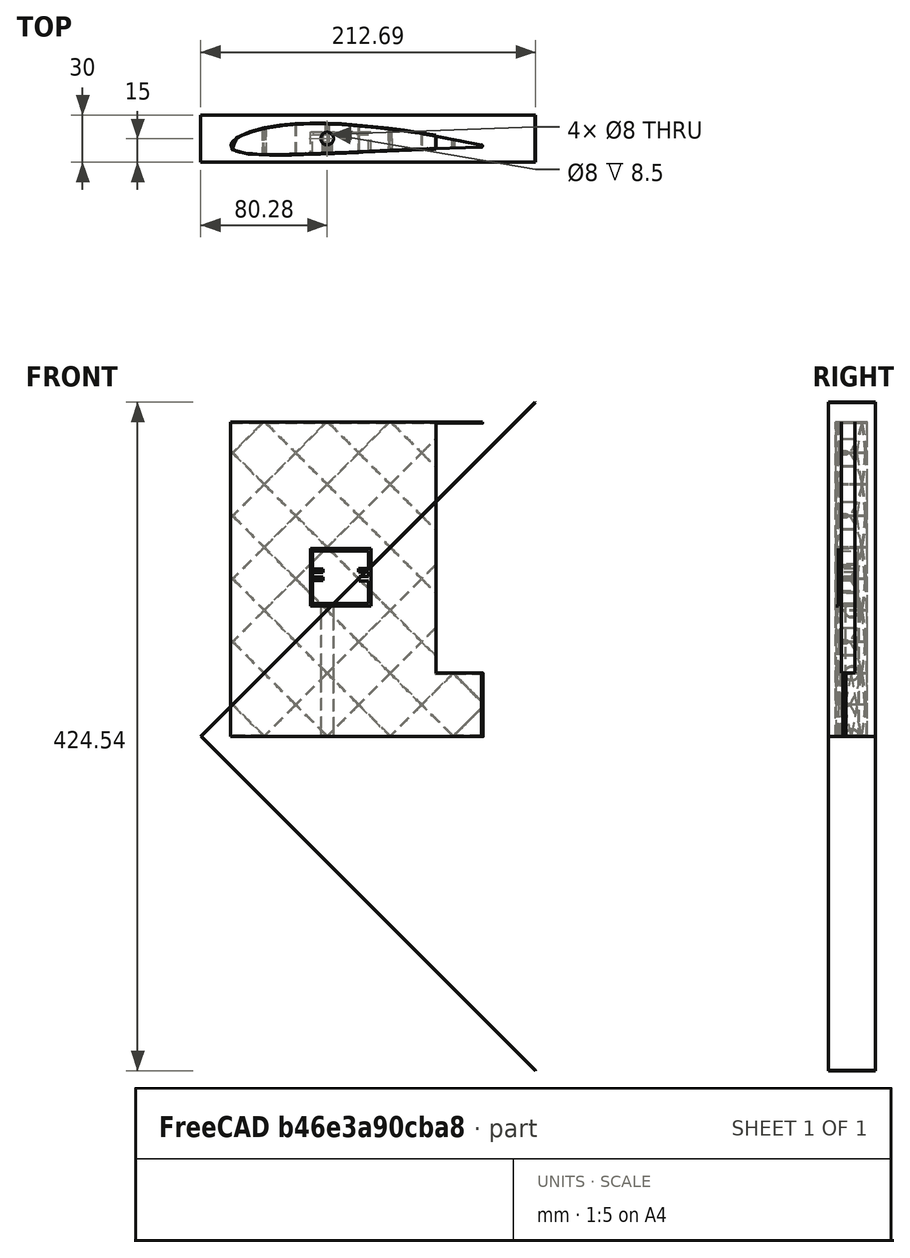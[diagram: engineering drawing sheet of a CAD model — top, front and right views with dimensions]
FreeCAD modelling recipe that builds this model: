
FCSTD DOCUMENT  (FreeCAD 0.21R33694 (Git))
Label: edge_wing
License: All rights reserved
LicenseURL: http://en.wikipedia.org/wiki/All_rights_reserved
objects: Sketcher::SketchObject×29, PartDesign::Pad×25, PartDesign::Body×19, Part::MultiFuse×13, Part::Cut×11, Part::MultiCommon×9, Part::Box×7, Part::Cylinder×7, PartDesign::Thickness×6, Part::FeaturePython×6, Part::Extrusion×2, PartDesign::FeatureBase×2
note: 161 computed .brp shape members not serialized (recipe doc carries the construction recipe); baked Part::Feature solids carry a one-line shape summary decoded from their .brp

FEATURE [Sketcher::SketchObject] Sketch006
  FullyConstrained = false
  MapMode = 5
  Support = -> [XY_Plane006]
  sketch-geometry (30):
    g0: ArcOfCircle CenterX=78.0455 CenterY=-4.69261 CenterZ=0 NormalX=0 NormalY=0 NormalZ=1 AngleXU=0 Radius=0.633228 StartAngle=4.68069 EndAngle=7.80443
    g1-g15: Circle x15 (B-spline internal-alignment scaffolding for g16; pole/knot coordinates omitted)
    g16: BSplineCurve PolesCount=15 KnotsCount=13 Degree=3 IsPeriodic=0
    g17-g29: GeomPoint x13 (B-spline internal-alignment scaffolding for g16; pole/knot coordinates omitted)
  constraints (6):
    c: Weight(g1) = 1
    c: Coincident(g16,g0)
    c: Equal(g1, g2-g15) x14
    c: Coincident(g16,g0)
    c: InternalAlignment(g1-g15 -> g16) x15
    c: InternalAlignment(g17-g29 -> g16) x13
FEATURE [PartDesign::Pad] Pad006
  Direction = (0,0,1)
  Length = 200
  Length2 = 10
  Profile = -> Sketch006
  ReferenceAxis = -> Sketch006 [N_Axis]
  Type = 0
FEATURE [PartDesign::Thickness] Thickness002
  Base = -> Pad006 [Face4,Face3]
  BaseFeature = -> Pad006
  Intersection = false
  Join = 0
  Mode = 1
  SupportTransform = false
  Value = 0.4
FEATURE [PartDesign::Body] Body006
  Group = -> [Sketch006,Pad006,Thickness002]
  Origin = -> Origin006
  Tip = -> Thickness002
FEATURE [Sketcher::SketchObject] Sketch007
  FullyConstrained = false
  MapMode = 5
  Support = -> [XY_Plane007]
  sketch-geometry (30):
    g0: ArcOfCircle CenterX=78.0455 CenterY=-4.69261 CenterZ=0 NormalX=0 NormalY=0 NormalZ=1 AngleXU=0 Radius=0.633228 StartAngle=4.68069 EndAngle=7.80443
    g1-g15: Circle x15 (B-spline internal-alignment scaffolding for g16; pole/knot coordinates omitted)
    g16: BSplineCurve PolesCount=15 KnotsCount=13 Degree=3 IsPeriodic=0
    g17-g29: GeomPoint x13 (B-spline internal-alignment scaffolding for g16; pole/knot coordinates omitted)
  constraints (6):
    c: Weight(g1) = 1
    c: Coincident(g16,g0)
    c: Equal(g1, g2-g15) x14
    c: Coincident(g16,g0)
    c: InternalAlignment(g1-g15 -> g16) x15
    c: InternalAlignment(g17-g29 -> g16) x13
FEATURE [PartDesign::Pad] Pad007
  Direction = (0,0,1)
  Length = 200
  Length2 = 10
  Profile = -> Sketch007
  ReferenceAxis = -> Sketch007 [N_Axis]
  Type = 0
FEATURE [PartDesign::Body] Body007
  Group = -> [Sketch007,Pad007]
  Origin = -> Origin007
  Tip = -> Pad007
FEATURE [Part::Box] Box004  label="Cube004"
  AttacherType = Attacher::AttachEngine3D
  Height = 0.4
  Length = 300
  Placement = pos=(-100,-15,0) rot=(0,1,0;0.785398rad)
  Width = 30
FEATURE [Part::FeaturePython] Array006  # Draft array (typed FeaturePython)
  AlwaysSyncPlacement = false
  Angle = 360
  ArrayType = 0
  Axis = (0,0,1)
  Base = -> Box004
  Center = (0,0,0)
  Count = 10
  ExpandArray = false
  Fuse = false
  IntervalAxis = (0,0,0)
  IntervalX = (100,0,0)
  IntervalY = (0,100,0)
  IntervalZ = (0,0,40)
  NumberCircles = 3
  NumberPolar = 5
  NumberX = 1
  NumberY = 1
  NumberZ = 10
  PlacementList = 10 placements: arithmetic series from (-100,-15,0) step (0,0,40) to (-100,-15,360)
  RadialDistance = 50
  ScaleList = (10) [(1,1,1),(1,1,1),(1,1,1),(1,1,1),(1,1,1),(1,1,1),(1,1,1),(1,1,1),(1,1,1),(1,1,1)]
  Symmetry = 1
  TangentialDistance = 25
FEATURE [Part::FeaturePython] Array007  # Draft array (typed FeaturePython)
  AlwaysSyncPlacement = false
  Angle = 360
  ArrayType = 0
  Axis = (0,0,1)
  Base = -> Array006
  Center = (0,0,0)
  Count = 9
  ExpandArray = false
  Fuse = false
  IntervalAxis = (0,0,0)
  IntervalX = (100,0,0)
  IntervalY = (0,100,0)
  IntervalZ = (0,0,40)
  NumberCircles = 3
  NumberPolar = 5
  NumberX = 1
  NumberY = 1
  NumberZ = 9
  PlacementList = 9 placements: arithmetic series from (0,0,0) step (0,0,40) to (0,0,320)
  RadialDistance = 50
  ScaleList = (9) [(1,1,1),(1,1,1),(1,1,1),(1,1,1),(1,1,1),(1,1,1),(1,1,1),(1,1,1),(1,1,1)]
  Symmetry = 1
  TangentialDistance = 25
FEATURE [Part::MultiCommon] Common005
  Shapes = -> [Body007,Array007]
FEATURE [Sketcher::SketchObject] Sketch008
  FullyConstrained = false
  MapMode = 5
  Support = -> [XY_Plane008]
  sketch-geometry (30):
    g0: ArcOfCircle CenterX=78.0455 CenterY=-4.69261 CenterZ=0 NormalX=0 NormalY=0 NormalZ=1 AngleXU=0 Radius=0.633228 StartAngle=4.68069 EndAngle=7.80443
    g1-g15: Circle x15 (B-spline internal-alignment scaffolding for g16; pole/knot coordinates omitted)
    g16: BSplineCurve PolesCount=15 KnotsCount=13 Degree=3 IsPeriodic=0
    g17-g29: GeomPoint x13 (B-spline internal-alignment scaffolding for g16; pole/knot coordinates omitted)
  constraints (6):
    c: Weight(g1) = 1
    c: Coincident(g16,g0)
    c: Equal(g1, g2-g15) x14
    c: Coincident(g16,g0)
    c: InternalAlignment(g1-g15 -> g16) x15
    c: InternalAlignment(g17-g29 -> g16) x13
FEATURE [PartDesign::Pad] Pad008
  Direction = (0,0,1)
  Length = 200
  Length2 = 10
  Profile = -> Sketch008
  ReferenceAxis = -> Sketch008 [N_Axis]
  Type = 0
FEATURE [PartDesign::Body] Body008
  Group = -> [Sketch008,Pad008]
  Origin = -> Origin008
  Tip = -> Pad008
FEATURE [Part::Box] Box005  label="Cube005"
  AttacherType = Attacher::AttachEngine3D
  Height = 0.4
  Length = 300
  Placement = pos=(-100,-15,0) rot=(0,-1,0;0.785398rad)
  Width = 30
FEATURE [Part::FeaturePython] Array008  # Draft array (typed FeaturePython)
  AlwaysSyncPlacement = false
  Angle = 360
  ArrayType = 0
  Axis = (0,0,1)
  Base = -> Box005
  Center = (0,0,0)
  Count = 20
  ExpandArray = false
  Fuse = false
  IntervalAxis = (0,0,0)
  IntervalX = (100,0,0)
  IntervalY = (0,100,0)
  IntervalZ = (0,0,40)
  NumberCircles = 3
  NumberPolar = 5
  NumberX = 1
  NumberY = 1
  NumberZ = 20
  Placement = pos=(0,1.90735e-05,-160) rot=(0,0,1;0rad)
  PlacementList = 20 placements: arithmetic series from (-100,-15,0) step (0,0,40) to (-100,-15,760)
  RadialDistance = 50
  ScaleList = (20) [(1,1,1),(1,1,1),(1,1,1),(1,1,1),(1,1,1),(1,1,1),(1,1,1),(1,1,1),(1,1,1),(1,1,1),(1,1,1),(1,1,1),(1,1,1),(1,1,1),(1,1,1),(1,1,1),(1,1,1),(1,1,1),(1,1,1),(1,1,1)]
  Symmetry = 1
  TangentialDistance = 25
FEATURE [Part::MultiCommon] Common004
  Shapes = -> [Body008,Array008]
FEATURE [Part::MultiFuse] Fusion004
  Shapes = -> [Common005,Common004]
FEATURE [Part::MultiFuse] Fusion005
  Shapes = -> [Body006,Fusion004]
FEATURE [Sketcher::SketchObject] Sketch015
  FullyConstrained = false
  MapMode = 5
  Placement = pos=(0,0,0) rot=(1,0,0;1.5708rad)
  sketch-geometry (4):
    g0: LineSegment StartX=0.4 StartY=0 StartZ=0 EndX=187.784 EndY=0 EndZ=0
    g1: LineSegment StartX=187.784 StartY=0 StartZ=0 EndX=187.784 EndY=-55.3386 EndZ=0
    g2: LineSegment StartX=187.784 StartY=-55.3386 StartZ=0 EndX=0.4 EndY=-55.3386 EndZ=0
    g3: LineSegment StartX=0.4 StartY=-55.3386 StartZ=0 EndX=0.4 EndY=0 EndZ=0
  constraints (8):
    c: Coincident(g0,g1)
    c: Coincident(g1,g2)
    c: Coincident(g2,g3)
    c: Coincident(g3,g0)
    c: Horizontal(g0)
    c: Horizontal(g2)
    c: Vertical(g1)
    c: Vertical(g3)
FEATURE [Part::Extrusion] Extrude
  Base = -> Sketch015
  Dir = (0,-1,-2e-16)
  DirMode = 2
  FaceMakerClass = Part::FaceMakerBullseye
  LengthFwd = 43
  LengthRev = 0
  Placement = pos=(49,20,40) rot=(0,-1,0;1.5708rad)
  Solid = true
  Symmetric = false
FEATURE [Part::Cut] Cut
  Base = -> Fusion005
  Tool = -> Extrude
FEATURE [Sketcher::SketchObject] Sketch010
  FullyConstrained = true
  MapMode = 5
  Support = -> [XY_Plane010]
  sketch-geometry (4):
    g0: LineSegment StartX=0 StartY=0 StartZ=0 EndX=160 EndY=0 EndZ=0
    g1: LineSegment StartX=160 StartY=0 StartZ=0 EndX=160 EndY=30 EndZ=0
    g2: LineSegment StartX=160 StartY=30 StartZ=0 EndX=0 EndY=30 EndZ=0
    g3: LineSegment StartX=0 StartY=30 StartZ=0 EndX=0 EndY=0 EndZ=0
  constraints (11):
    c: Coincident(g0,g1)
    c: Coincident(g1,g2)
    c: Coincident(g2,g3)
    c: Coincident(g3,g0)
    c: Horizontal(g0)
    c: Horizontal(g2)
    c: Vertical(g1)
    c: Vertical(g3)
    c: Coincident(g0,g-1)
    c: DistanceX(g2,g2) = 160
    c: DistanceY(g1,g1) = 30
FEATURE [PartDesign::Pad] Pad010
  Direction = (0,0,1)
  Length = 0.4
  Length2 = 10
  Profile = -> Sketch010
  ReferenceAxis = -> Sketch010 [N_Axis]
  Type = 0
FEATURE [Sketcher::SketchObject] Sketch011
  ExternalGeometry = -> [Pad010]
  FullyConstrained = true
  MapMode = 5
  Placement = pos=(0,0,0) rot=(1,0,0;3.14159rad)
  Support = -> [Pad010]
  sketch-geometry (4):
    g0: LineSegment StartX=0 StartY=0 StartZ=0 EndX=0.4 EndY=0 EndZ=0
    g1: LineSegment StartX=0.4 StartY=0 StartZ=0 EndX=0.4 EndY=-30 EndZ=0
    g2: LineSegment StartX=0.4 StartY=-30 StartZ=0 EndX=0 EndY=-30 EndZ=0
    g3: LineSegment StartX=0 StartY=-30 StartZ=0 EndX=0 EndY=0 EndZ=0
  constraints (11):
    c: Coincident(g0,g1)
    c: Coincident(g1,g2)
    c: Coincident(g2,g3)
    c: Coincident(g3,g0)
    c: Horizontal(g0)
    c: Horizontal(g2)
    c: Vertical(g1)
    c: Vertical(g3)
    c: Coincident(g0,g-1)
    c: DistanceY(g-3,g2) = 0
    c: DistanceX(g0,g0) = 0.4
FEATURE [PartDesign::Pad] Pad011
  BaseFeature = -> Pad010
  Direction = (0,0,-1)
  Length = 30
  Length2 = 10
  Profile = -> Sketch011
  ReferenceAxis = -> Sketch011 [N_Axis]
  Type = 0
FEATURE [Sketcher::SketchObject] Sketch014
  FullyConstrained = true
  MapMode = 5
  Placement = pos=(0,0,0) rot=(1,0,0;1.5708rad)
  Support = -> [XZ_Plane009]
FEATURE [PartDesign::Body] Body009
  Group = -> [Sketch010,Pad010,Sketch011,Pad011,Sketch014]
  Origin = -> Origin009
  Placement = pos=(49,-16,40) rot=(0,-1,0;1.5708rad)
  Tip = -> Pad011
FEATURE [Sketcher::SketchObject] Sketch009
  FullyConstrained = false
  MapMode = 5
  sketch-geometry (30):
    g0: ArcOfCircle CenterX=78.0455 CenterY=-4.69261 CenterZ=0 NormalX=0 NormalY=0 NormalZ=1 AngleXU=0 Radius=0.633228 StartAngle=4.68069 EndAngle=7.80443
    g1-g15: Circle x15 (B-spline internal-alignment scaffolding for g16; pole/knot coordinates omitted)
    g16: BSplineCurve PolesCount=15 KnotsCount=13 Degree=3 IsPeriodic=0
    g17-g29: GeomPoint x13 (B-spline internal-alignment scaffolding for g16; pole/knot coordinates omitted)
  constraints (6):
    c: Weight(g1) = 1
    c: Coincident(g16,g0)
    c: Equal(g1, g2-g15) x14
    c: Coincident(g16,g0)
    c: InternalAlignment(g1-g15 -> g16) x15
    c: InternalAlignment(g17-g29 -> g16) x13
FEATURE [PartDesign::Pad] Pad009
  Direction = (0,0,1)
  Length = 200
  Length2 = 10
  Profile = -> Sketch009
  ReferenceAxis = -> Sketch009 [N_Axis]
  Type = 0
FEATURE [Part::MultiCommon] Common006
  Shapes = -> [Body009,Pad009]
FEATURE [Part::MultiFuse] Fusion006
  Shapes = -> [Cut,Common006]
FEATURE [Sketcher::SketchObject] Sketch018
  FullyConstrained = false
  MapMode = 5
  Support = -> [XY_Plane002]
  sketch-geometry (4):
    g0: LineSegment StartX=-7.74956 StartY=27.0881 StartZ=0 EndX=30.8607 EndY=27.0881 EndZ=0
    g1: LineSegment StartX=30.8607 StartY=27.0881 StartZ=0 EndX=30.8607 EndY=-9.4314 EndZ=0
    g2: LineSegment StartX=30.8607 StartY=-9.4314 StartZ=0 EndX=-7.74956 EndY=-9.4314 EndZ=0
    g3: LineSegment StartX=-7.74956 StartY=-9.4314 StartZ=0 EndX=-7.74956 EndY=27.0881 EndZ=0
  constraints (8):
    c: Coincident(g0,g1)
    c: Coincident(g1,g2)
    c: Coincident(g2,g3)
    c: Coincident(g3,g0)
    c: Horizontal(g0)
    c: Horizontal(g2)
    c: Vertical(g1)
    c: Vertical(g3)
FEATURE [PartDesign::Pad] Pad012
  Direction = (0,0,1)
  Length = 14
  Length2 = 10
  Profile = -> Sketch018
  ReferenceAxis = -> Sketch018 [N_Axis]
  Type = 0
FEATURE [PartDesign::Body] Body002
  Group = -> [Sketch018,Pad012]
  Origin = -> Origin002
  Placement = pos=(0,4,110) rot=(0,0.707107,-0.707107;3.14159rad)
  Tip = -> Pad012
FEATURE [Sketcher::SketchObject] Sketch017
  FullyConstrained = false
  MapMode = 5
  Support = -> [XY_Plane001]
  sketch-geometry (4):
    g0: LineSegment StartX=-7.74956 StartY=27.0881 StartZ=0 EndX=30.8607 EndY=27.0881 EndZ=0
    g1: LineSegment StartX=30.8607 StartY=27.0881 StartZ=0 EndX=30.8607 EndY=-9.4314 EndZ=0
    g2: LineSegment StartX=30.8607 StartY=-9.4314 StartZ=0 EndX=-7.74956 EndY=-9.4314 EndZ=0
    g3: LineSegment StartX=-7.74956 StartY=-9.4314 StartZ=0 EndX=-7.74956 EndY=27.0881 EndZ=0
  constraints (8):
    c: Coincident(g0,g1)
    c: Coincident(g1,g2)
    c: Coincident(g2,g3)
    c: Coincident(g3,g0)
    c: Horizontal(g0)
    c: Horizontal(g2)
    c: Vertical(g1)
    c: Vertical(g3)
FEATURE [PartDesign::Pad] Pad013
  Direction = (0,0,1)
  Length = 14
  Length2 = 10
  Profile = -> Sketch017
  ReferenceAxis = -> Sketch017 [N_Axis]
  Type = 0
FEATURE [PartDesign::Thickness] Thickness
  Base = -> Pad013 [Face6]
  BaseFeature = -> Pad013
  Intersection = false
  Join = 1
  Mode = 0
  Reversed = true
  SupportTransform = false
  Value = 1.6
FEATURE [Sketcher::SketchObject] Sketch021
  ExternalGeometry = -> [Thickness]
  FullyConstrained = false
  MapMode = 5
  Placement = pos=(0,0,1.6) rot=(0,0,1;0rad)
  Support = -> [Thickness]
  sketch-geometry (16):
    g0: LineSegment StartX=-6.14956 StartY=10.9638 StartZ=0 EndX=-0.106128 EndY=10.9638 EndZ=0
    g1: LineSegment StartX=-0.106128 StartY=10.9638 StartZ=0 EndX=-0.106128 EndY=8.15304 EndZ=0
    g2: LineSegment StartX=-0.106128 StartY=8.15304 StartZ=0 EndX=-6.14956 EndY=8.15304 EndZ=0
    g3: LineSegment StartX=-6.14956 StartY=8.15304 StartZ=0 EndX=-6.14956 EndY=10.9638 EndZ=0
    g4: LineSegment StartX=-6.14956 StartY=3.3087 StartZ=0 EndX=0 EndY=3.3087 EndZ=0
    g5: LineSegment StartX=0 StartY=3.3087 StartZ=0 EndX=0 EndY=5.33627 EndZ=0
    g6: LineSegment StartX=0 StartY=5.33627 StartZ=0 EndX=-6.14956 EndY=5.33627 EndZ=0
    g7: LineSegment StartX=-6.14956 StartY=5.33627 StartZ=0 EndX=-6.14956 EndY=3.3087 EndZ=0
    g8: LineSegment StartX=29.2607 StartY=10.6733 StartZ=0 EndX=22.6404 EndY=10.6733 EndZ=0
    g9: LineSegment StartX=22.6404 StartY=10.6733 StartZ=0 EndX=22.6404 EndY=8.47828 EndZ=0
    g10: LineSegment StartX=22.6404 StartY=8.47828 StartZ=0 EndX=29.2607 EndY=8.47828 EndZ=0
    g11: LineSegment StartX=29.2607 StartY=8.47828 StartZ=0 EndX=29.2607 EndY=10.6733 EndZ=0
    g12: LineSegment StartX=29.2607 StartY=5.57967 StartZ=0 EndX=22.6404 EndY=5.57967 EndZ=0
    g13: LineSegment StartX=22.6404 StartY=5.57967 StartZ=0 EndX=22.6404 EndY=3.49718 EndZ=0
    g14: LineSegment StartX=22.6404 StartY=3.49718 StartZ=0 EndX=29.2607 EndY=3.49718 EndZ=0
    g15: LineSegment StartX=29.2607 StartY=3.49718 StartZ=0 EndX=29.2607 EndY=5.57967 EndZ=0
  constraints (37):
    c: Coincident(g0,g1)
    c: Coincident(g1,g2)
    c: Coincident(g2,g3)
    c: Coincident(g3,g0)
    c: Horizontal(g0)
    c: Horizontal(g2)
    c: Vertical(g1)
    c: Vertical(g3)
    c: PointOnObject(g0,g-3)
    c: Coincident(g4,g5)
    c: Coincident(g5,g6)
    c: Coincident(g6,g7)
    c: Coincident(g7,g4)
    c: Horizontal(g4)
    c: Horizontal(g6)
    c: Vertical(g5)
    c: Vertical(g7)
    c: PointOnObject(g4,g-3)
    c: PointOnObject(g5,g-2)
    c: Coincident(g8,g9)
    c: Coincident(g9,g10)
    c: Coincident(g10,g11)
    c: Coincident(g11,g8)
    c: Horizontal(g8)
    c: Horizontal(g10)
    c: Vertical(g9)
    c: Vertical(g11)
    c: PointOnObject(g8,g-4)
    c: Coincident(g12,g13)
    c: Coincident(g13,g14)
    c: Coincident(g14,g15)
    c: Coincident(g15,g12)
    c: Horizontal(g12)
    c: Horizontal(g14)
    c: Vertical(g13)
    c: Vertical(g15)
    c: PointOnObject(g12,g-4)
FEATURE [PartDesign::Pad] Pad014
  BaseFeature = -> Thickness
  Direction = (0,0,1)
  Length = 12.4
  Length2 = 10
  Profile = -> Sketch021
  ReferenceAxis = -> Sketch021 [N_Axis]
  Type = 0
FEATURE [PartDesign::Body] Body001
  Group = -> [Sketch017,Pad013,Thickness,Sketch021,Pad014]
  Origin = -> Origin001
  Placement = pos=(0,4,110) rot=(0,-0.707107,0.707107;3.14159rad)
  Tip = -> Pad014
FEATURE [Part::Cut] Cut001
  Base = -> Fusion006
  Tool = -> Body002
FEATURE [Sketcher::SketchObject] Sketch022
  FullyConstrained = false
  MapMode = 5
  Support = -> [XY_Plane011]
  sketch-geometry (30):
    g0: ArcOfCircle CenterX=78.0455 CenterY=-4.69261 CenterZ=0 NormalX=0 NormalY=0 NormalZ=1 AngleXU=0 Radius=0.633228 StartAngle=4.68069 EndAngle=7.80443
    g1-g15: Circle x15 (B-spline internal-alignment scaffolding for g16; pole/knot coordinates omitted)
    g16: BSplineCurve PolesCount=15 KnotsCount=13 Degree=3 IsPeriodic=0
    g17-g29: GeomPoint x13 (B-spline internal-alignment scaffolding for g16; pole/knot coordinates omitted)
  constraints (6):
    c: Weight(g1) = 1
    c: Coincident(g16,g0)
    c: Equal(g1, g2-g15) x14
    c: Coincident(g16,g0)
    c: InternalAlignment(g1-g15 -> g16) x15
    c: InternalAlignment(g17-g29 -> g16) x13
FEATURE [PartDesign::Pad] Pad015
  Direction = (0,0,1)
  Length = 200
  Length2 = 10
  Profile = -> Sketch022
  ReferenceAxis = -> Sketch022 [N_Axis]
  Type = 0
FEATURE [Part::MultiCommon] Common
  Shapes = -> [Body001,Pad015]
FEATURE [Part::Cylinder] Cylinder003
  Angle = 360
  AttacherType = Attacher::AttachEngine3D
  FirstAngle = 0
  Height = 84.5
  Placement = pos=(-20,0,0) rot=(0,0,1;0rad)
  Radius = 4
  SecondAngle = 0
FEATURE [PartDesign::FeatureBase] BaseFeature
  BaseFeature = -> Cylinder003
FEATURE [PartDesign::Thickness] Thickness001
  Base = -> BaseFeature [Face3,Face2]
  BaseFeature = -> BaseFeature
  Intersection = false
  Join = 0
  Mode = 1
  SupportTransform = false
  Value = 0.4
FEATURE [PartDesign::Body] Body003
  BaseFeature = -> Cylinder003
  Group = -> [BaseFeature,Thickness001]
  Origin = -> Origin003
  Placement = pos=(-20,0,0) rot=(0,0,1;0rad)
  Tip = -> Thickness001
FEATURE [Part::Cylinder] Cylinder002
  Angle = 360
  AttacherType = Attacher::AttachEngine3D
  FirstAngle = 0
  Height = 200
  Placement = pos=(-20,0,0) rot=(0,0,1;0rad)
  Radius = 4
  SecondAngle = 0
FEATURE [Sketcher::SketchObject] Sketch004
  FullyConstrained = false
  MapMode = 5
  Support = -> [XY_Plane005]
  sketch-geometry (30):
    g0: ArcOfCircle CenterX=78.0455 CenterY=-4.69261 CenterZ=0 NormalX=0 NormalY=0 NormalZ=1 AngleXU=0 Radius=0.633228 StartAngle=4.68069 EndAngle=7.80443
    g1-g15: Circle x15 (B-spline internal-alignment scaffolding for g16; pole/knot coordinates omitted)
    g16: BSplineCurve PolesCount=15 KnotsCount=13 Degree=3 IsPeriodic=0
    g17-g29: GeomPoint x13 (B-spline internal-alignment scaffolding for g16; pole/knot coordinates omitted)
  constraints (6):
    c: Weight(g1) = 1
    c: Coincident(g16,g0)
    c: Equal(g1, g2-g15) x14
    c: Coincident(g16,g0)
    c: InternalAlignment(g1-g15 -> g16) x15
    c: InternalAlignment(g17-g29 -> g16) x13
FEATURE [PartDesign::Pad] Pad004
  Direction = (1,1,1)
  Length = 0.8
  Length2 = 100
  Profile = -> Sketch004
  Type = 0
FEATURE [PartDesign::Body] Body005
  Group = -> [Sketch004,Pad004]
  Origin = -> Origin005
  Tip = -> Pad004
FEATURE [Part::Cut] Cut002
  Base = -> Body005
  Placement = pos=(0,0,199.2) rot=(0,0,1;0rad)
  Tool = -> Cylinder002
FEATURE [Part::Cylinder] Cylinder001
  Angle = 360
  AttacherType = Attacher::AttachEngine3D
  FirstAngle = 0
  Height = 200
  Placement = pos=(-20,0,0) rot=(0,0,1;0rad)
  Radius = 4
  SecondAngle = 0
FEATURE [Sketcher::SketchObject] Sketch003
  FullyConstrained = false
  MapMode = 5
  Support = -> [XY_Plane004]
  sketch-geometry (30):
    g0: ArcOfCircle CenterX=78.0455 CenterY=-4.69261 CenterZ=0 NormalX=0 NormalY=0 NormalZ=1 AngleXU=0 Radius=0.633228 StartAngle=4.68069 EndAngle=7.80443
    g1-g15: Circle x15 (B-spline internal-alignment scaffolding for g16; pole/knot coordinates omitted)
    g16: BSplineCurve PolesCount=15 KnotsCount=13 Degree=3 IsPeriodic=0
    g17-g29: GeomPoint x13 (B-spline internal-alignment scaffolding for g16; pole/knot coordinates omitted)
  constraints (6):
    c: Weight(g1) = 1
    c: Coincident(g16,g0)
    c: Equal(g1, g2-g15) x14
    c: Coincident(g16,g0)
    c: InternalAlignment(g1-g15 -> g16) x15
    c: InternalAlignment(g17-g29 -> g16) x13
FEATURE [PartDesign::Pad] Pad003
  Direction = (1,1,1)
  Length = 0.8
  Length2 = 100
  Profile = -> Sketch003
  Type = 0
FEATURE [PartDesign::Body] Body004
  Group = -> [Sketch003,Pad003]
  Origin = -> Origin004
  Tip = -> Pad003
FEATURE [Part::Cut] Cut003
  Base = -> Body004
  Tool = -> Cylinder001
FEATURE [Part::MultiFuse] Fusion
  Shapes = -> [Common,Cut001]
FEATURE [Part::Cylinder] Cylinder004
  Angle = 360
  AttacherType = Attacher::AttachEngine3D
  FirstAngle = 0
  Height = 84.5
  Placement = pos=(-20,0,0) rot=(0,0,1;0rad)
  Radius = 4
  SecondAngle = 0
FEATURE [Part::Cut] Cut004
  Base = -> Fusion
  Tool = -> Cylinder004
FEATURE [Part::Box] Box  label="Cube"
  AttacherType = Attacher::AttachEngine3D
  Height = 20
  Length = 40
  Placement = pos=(49,-7,196) rot=(0,0,1;0rad)
  Width = 10
FEATURE [Sketcher::SketchObject] Sketch023
  FullyConstrained = false
  MapMode = 5
  Support = -> [XY_Plane012]
  sketch-geometry (30):
    g0: ArcOfCircle CenterX=78.0455 CenterY=-4.69261 CenterZ=0 NormalX=0 NormalY=0 NormalZ=1 AngleXU=0 Radius=0.633228 StartAngle=4.68069 EndAngle=7.80443
    g1-g15: Circle x15 (B-spline internal-alignment scaffolding for g16; pole/knot coordinates omitted)
    g16: BSplineCurve PolesCount=15 KnotsCount=13 Degree=3 IsPeriodic=0
    g17-g29: GeomPoint x13 (B-spline internal-alignment scaffolding for g16; pole/knot coordinates omitted)
  constraints (6):
    c: Weight(g1) = 1
    c: Coincident(g16,g0)
    c: Equal(g1, g2-g15) x14
    c: Coincident(g16,g0)
    c: InternalAlignment(g1-g15 -> g16) x15
    c: InternalAlignment(g17-g29 -> g16) x13
FEATURE [PartDesign::Pad] Pad016
  Direction = (1,1,1)
  Length = 0.8
  Length2 = 100
  Profile = -> Sketch023
  Type = 0
FEATURE [PartDesign::Body] Body010
  Group = -> [Sketch023,Pad016]
  Origin = -> Origin010
  Placement = pos=(0,0,199.2) rot=(0,0,1;0rad)
  Tip = -> Pad016
FEATURE [Part::Cut] Cut005
  Base = -> Body010
  Tool = -> Box
FEATURE [Part::MultiFuse] Fusion007
  Shapes = -> [Cut005,Cut003,Cut004]
FEATURE [Part::MultiFuse] Fusion008
  Shapes = -> [Body003,Fusion007]
FEATURE [Part::Box] Box006  label="Cube006"
  AttacherType = Attacher::AttachEngine3D
  Height = 0.8
  Length = 50
  Placement = pos=(48.6,-10.8,39.6) rot=(0,0,1;0rad)
  Width = 30
FEATURE [Part::Box] Box007  label="Cube007"
  AttacherType = Attacher::AttachEngine3D
  Height = 20
  Length = 40
  Placement = pos=(49,-7,196) rot=(0,0,1;0rad)
  Width = 10
FEATURE [Part::Box] Box008  label="Cube008"
  AttacherType = Attacher::AttachEngine3D
  Height = 0.4
  Length = 300
  Placement = pos=(-100,-15,0) rot=(0,1,0;0.785398rad)
  Width = 30
FEATURE [Part::FeaturePython] Array009  # Draft array (typed FeaturePython)
  AlwaysSyncPlacement = false
  Angle = 360
  ArrayType = 0
  Axis = (0,0,1)
  Base = -> Box008
  Center = (0,0,0)
  Count = 10
  ExpandArray = false
  Fuse = false
  IntervalAxis = (0,0,0)
  IntervalX = (100,0,0)
  IntervalY = (0,100,0)
  IntervalZ = (0,0,40)
  NumberCircles = 3
  NumberPolar = 5
  NumberX = 1
  NumberY = 1
  NumberZ = 10
  PlacementList = 10 placements: arithmetic series from (-100,-15,0) step (0,0,40) to (-100,-15,360)
  RadialDistance = 50
  ScaleList = (10) [(1,1,1),(1,1,1),(1,1,1),(1,1,1),(1,1,1),(1,1,1),(1,1,1),(1,1,1),(1,1,1),(1,1,1)]
  Symmetry = 1
  TangentialDistance = 25
FEATURE [Part::FeaturePython] Array010  # Draft array (typed FeaturePython)
  AlwaysSyncPlacement = false
  Angle = 360
  ArrayType = 0
  Axis = (0,0,1)
  Base = -> Array009
  Center = (0,0,0)
  Count = 9
  ExpandArray = false
  Fuse = false
  IntervalAxis = (0,0,0)
  IntervalX = (100,0,0)
  IntervalY = (0,100,0)
  IntervalZ = (0,0,40)
  NumberCircles = 3
  NumberPolar = 5
  NumberX = 1
  NumberY = 1
  NumberZ = 9
  PlacementList = 9 placements: arithmetic series from (0,0,0) step (0,0,40) to (0,0,320)
  RadialDistance = 50
  ScaleList = (9) [(1,1,1),(1,1,1),(1,1,1),(1,1,1),(1,1,1),(1,1,1),(1,1,1),(1,1,1),(1,1,1)]
  Symmetry = 1
  TangentialDistance = 25
FEATURE [Part::Box] Box009  label="Cube009"
  AttacherType = Attacher::AttachEngine3D
  Height = 0.4
  Length = 300
  Placement = pos=(-100,-15,0) rot=(0,-1,0;0.785398rad)
  Width = 30
FEATURE [Part::FeaturePython] Array011  # Draft array (typed FeaturePython)
  AlwaysSyncPlacement = false
  Angle = 360
  ArrayType = 0
  Axis = (0,0,1)
  Base = -> Box009
  Center = (0,0,0)
  Count = 20
  ExpandArray = false
  Fuse = false
  IntervalAxis = (0,0,0)
  IntervalX = (100,0,0)
  IntervalY = (0,100,0)
  IntervalZ = (0,0,40)
  NumberCircles = 3
  NumberPolar = 5
  NumberX = 1
  NumberY = 1
  NumberZ = 20
  Placement = pos=(0,1.90735e-05,-160) rot=(0,0,1;0rad)
  PlacementList = 20 placements: arithmetic series from (-100,-15,0) step (0,0,40) to (-100,-15,760)
  RadialDistance = 50
  ScaleList = (20) [(1,1,1),(1,1,1),(1,1,1),(1,1,1),(1,1,1),(1,1,1),(1,1,1),(1,1,1),(1,1,1),(1,1,1),(1,1,1),(1,1,1),(1,1,1),(1,1,1),(1,1,1),(1,1,1),(1,1,1),(1,1,1),(1,1,1),(1,1,1)]
  Symmetry = 1
  TangentialDistance = 25
FEATURE [Part::Cylinder] Cylinder005
  Angle = 360
  AttacherType = Attacher::AttachEngine3D
  FirstAngle = 0
  Height = 200
  Placement = pos=(-20,0,0) rot=(0,0,1;0rad)
  Radius = 4
  SecondAngle = 0
FEATURE [Part::Cylinder] Cylinder006
  Angle = 360
  AttacherType = Attacher::AttachEngine3D
  FirstAngle = 0
  Height = 84.5
  Placement = pos=(-20,0,0) rot=(0,0,1;0rad)
  Radius = 4
  SecondAngle = 0
FEATURE [PartDesign::FeatureBase] BaseFeature001
  BaseFeature = -> Cylinder006
FEATURE [Part::Cylinder] Cylinder007
  Angle = 360
  AttacherType = Attacher::AttachEngine3D
  FirstAngle = 0
  Height = 84.5
  Placement = pos=(-20,0,0) rot=(0,0,1;0rad)
  Radius = 4
  SecondAngle = 0
FEATURE [Sketcher::SketchObject] Sketch024
  FullyConstrained = false
  MapMode = 5
  Support = -> [XY_Plane016]
  sketch-geometry (30):
    g0: ArcOfCircle CenterX=78.0455 CenterY=-4.69261 CenterZ=0 NormalX=0 NormalY=0 NormalZ=1 AngleXU=0 Radius=0.633228 StartAngle=4.68069 EndAngle=7.80443
    g1-g15: Circle x15 (B-spline internal-alignment scaffolding for g16; pole/knot coordinates omitted)
    g16: BSplineCurve PolesCount=15 KnotsCount=13 Degree=3 IsPeriodic=0
    g17-g29: GeomPoint x13 (B-spline internal-alignment scaffolding for g16; pole/knot coordinates omitted)
  constraints (6):
    c: Weight(g1) = 1
    c: Coincident(g16,g0)
    c: Equal(g1, g2-g15) x14
    c: Coincident(g16,g0)
    c: InternalAlignment(g1-g15 -> g16) x15
    c: InternalAlignment(g17-g29 -> g16) x13
FEATURE [PartDesign::Pad] Pad017
  Direction = (1,1,1)
  Length = 0.8
  Length2 = 100
  Profile = -> Sketch024
  Type = 0
FEATURE [PartDesign::Body] Body014
  Group = -> [Sketch024,Pad017]
  Origin = -> Origin014
  Tip = -> Pad017
FEATURE [Part::Cut] Cut008
  Base = -> Body014
  Tool = -> Cylinder005
FEATURE [Sketcher::SketchObject] Sketch025
  FullyConstrained = false
  MapMode = 5
  Support = -> [XY_Plane017]
  sketch-geometry (30):
    g0: ArcOfCircle CenterX=78.0455 CenterY=-4.69261 CenterZ=0 NormalX=0 NormalY=0 NormalZ=1 AngleXU=0 Radius=0.633228 StartAngle=4.68069 EndAngle=7.80443
    g1-g15: Circle x15 (B-spline internal-alignment scaffolding for g16; pole/knot coordinates omitted)
    g16: BSplineCurve PolesCount=15 KnotsCount=13 Degree=3 IsPeriodic=0
    g17-g29: GeomPoint x13 (B-spline internal-alignment scaffolding for g16; pole/knot coordinates omitted)
  constraints (6):
    c: Weight(g1) = 1
    c: Coincident(g16,g0)
    c: Equal(g1, g2-g15) x14
    c: Coincident(g16,g0)
    c: InternalAlignment(g1-g15 -> g16) x15
    c: InternalAlignment(g17-g29 -> g16) x13
FEATURE [PartDesign::Pad] Pad018
  Direction = (0,0,1)
  Length = 200
  Length2 = 10
  Profile = -> Sketch025
  ReferenceAxis = -> Sketch025 [N_Axis]
  Type = 0
FEATURE [Sketcher::SketchObject] Sketch026
  FullyConstrained = false
  MapMode = 5
  Support = -> [XY_Plane018]
  sketch-geometry (30):
    g0: ArcOfCircle CenterX=78.0455 CenterY=-4.69261 CenterZ=0 NormalX=0 NormalY=0 NormalZ=1 AngleXU=0 Radius=0.633228 StartAngle=4.68069 EndAngle=7.80443
    g1-g15: Circle x15 (B-spline internal-alignment scaffolding for g16; pole/knot coordinates omitted)
    g16: BSplineCurve PolesCount=15 KnotsCount=13 Degree=3 IsPeriodic=0
    g17-g29: GeomPoint x13 (B-spline internal-alignment scaffolding for g16; pole/knot coordinates omitted)
  constraints (6):
    c: Weight(g1) = 1
    c: Coincident(g16,g0)
    c: Equal(g1, g2-g15) x14
    c: Coincident(g16,g0)
    c: InternalAlignment(g1-g15 -> g16) x15
    c: InternalAlignment(g17-g29 -> g16) x13
FEATURE [PartDesign::Pad] Pad019
  Direction = (0,0,1)
  Length = 200
  Length2 = 10
  Profile = -> Sketch026
  ReferenceAxis = -> Sketch026 [N_Axis]
  Type = 0
FEATURE [PartDesign::Body] Body016
  Group = -> [Sketch026,Pad019]
  Origin = -> Origin016
  Tip = -> Pad019
FEATURE [Part::MultiCommon] Common009
  Shapes = -> [Body016,Array010]
FEATURE [Sketcher::SketchObject] Sketch027
  FullyConstrained = false
  MapMode = 5
  Support = -> [XY_Plane019]
  sketch-geometry (30):
    g0: ArcOfCircle CenterX=78.0455 CenterY=-4.69261 CenterZ=0 NormalX=0 NormalY=0 NormalZ=1 AngleXU=0 Radius=0.633228 StartAngle=4.68069 EndAngle=7.80443
    g1-g15: Circle x15 (B-spline internal-alignment scaffolding for g16; pole/knot coordinates omitted)
    g16: BSplineCurve PolesCount=15 KnotsCount=13 Degree=3 IsPeriodic=0
    g17-g29: GeomPoint x13 (B-spline internal-alignment scaffolding for g16; pole/knot coordinates omitted)
  constraints (6):
    c: Weight(g1) = 1
    c: Coincident(g16,g0)
    c: Equal(g1, g2-g15) x14
    c: Coincident(g16,g0)
    c: InternalAlignment(g1-g15 -> g16) x15
    c: InternalAlignment(g17-g29 -> g16) x13
FEATURE [PartDesign::Pad] Pad020
  Direction = (0,0,1)
  Length = 200
  Length2 = 10
  Profile = -> Sketch027
  ReferenceAxis = -> Sketch027 [N_Axis]
  Type = 0
FEATURE [PartDesign::Body] Body017
  Group = -> [Sketch027,Pad020]
  Origin = -> Origin017
  Tip = -> Pad020
FEATURE [Part::MultiCommon] Common008
  Shapes = -> [Body017,Array011]
FEATURE [Part::MultiFuse] Fusion010
  Shapes = -> [Common009,Common008]
FEATURE [Sketcher::SketchObject] Sketch028
  FullyConstrained = false
  MapMode = 5
  sketch-geometry (30):
    g0: ArcOfCircle CenterX=78.0455 CenterY=-4.69261 CenterZ=0 NormalX=0 NormalY=0 NormalZ=1 AngleXU=0 Radius=0.633228 StartAngle=4.68069 EndAngle=7.80443
    g1-g15: Circle x15 (B-spline internal-alignment scaffolding for g16; pole/knot coordinates omitted)
    g16: BSplineCurve PolesCount=15 KnotsCount=13 Degree=3 IsPeriodic=0
    g17-g29: GeomPoint x13 (B-spline internal-alignment scaffolding for g16; pole/knot coordinates omitted)
  constraints (6):
    c: Weight(g1) = 1
    c: Coincident(g16,g0)
    c: Equal(g1, g2-g15) x14
    c: Coincident(g16,g0)
    c: InternalAlignment(g1-g15 -> g16) x15
    c: InternalAlignment(g17-g29 -> g16) x13
FEATURE [PartDesign::Pad] Pad021
  Direction = (0,0,1)
  Length = 200
  Length2 = 10
  Profile = -> Sketch028
  ReferenceAxis = -> Sketch028 [N_Axis]
  Type = 0
FEATURE [Sketcher::SketchObject] Sketch029
  FullyConstrained = true
  MapMode = 5
  Support = -> [XY_Plane020]
  sketch-geometry (4):
    g0: LineSegment StartX=0 StartY=0 StartZ=0 EndX=160 EndY=0 EndZ=0
    g1: LineSegment StartX=160 StartY=0 StartZ=0 EndX=160 EndY=30 EndZ=0
    g2: LineSegment StartX=160 StartY=30 StartZ=0 EndX=0 EndY=30 EndZ=0
    g3: LineSegment StartX=0 StartY=30 StartZ=0 EndX=0 EndY=0 EndZ=0
  constraints (11):
    c: Coincident(g0,g1)
    c: Coincident(g1,g2)
    c: Coincident(g2,g3)
    c: Coincident(g3,g0)
    c: Horizontal(g0)
    c: Horizontal(g2)
    c: Vertical(g1)
    c: Vertical(g3)
    c: Coincident(g0,g-1)
    c: DistanceX(g2,g2) = 160
    c: DistanceY(g1,g1) = 30
FEATURE [PartDesign::Pad] Pad022
  Direction = (0,0,1)
  Length = 0.4
  Length2 = 10
  Profile = -> Sketch029
  ReferenceAxis = -> Sketch029 [N_Axis]
  Type = 0
FEATURE [Sketcher::SketchObject] Sketch030
  ExternalGeometry = -> [Pad022]
  FullyConstrained = true
  MapMode = 5
  Placement = pos=(0,0,0) rot=(1,0,0;3.14159rad)
  Support = -> [Pad022]
  sketch-geometry (4):
    g0: LineSegment StartX=0 StartY=0 StartZ=0 EndX=0.4 EndY=0 EndZ=0
    g1: LineSegment StartX=0.4 StartY=0 StartZ=0 EndX=0.4 EndY=-30 EndZ=0
    g2: LineSegment StartX=0.4 StartY=-30 StartZ=0 EndX=0 EndY=-30 EndZ=0
    g3: LineSegment StartX=0 StartY=-30 StartZ=0 EndX=0 EndY=0 EndZ=0
  constraints (11):
    c: Coincident(g0,g1)
    c: Coincident(g1,g2)
    c: Coincident(g2,g3)
    c: Coincident(g3,g0)
    c: Horizontal(g0)
    c: Horizontal(g2)
    c: Vertical(g1)
    c: Vertical(g3)
    c: Coincident(g0,g-1)
    c: DistanceY(g-3,g2) = 0
    c: DistanceX(g0,g0) = 0.4
FEATURE [PartDesign::Pad] Pad023
  BaseFeature = -> Pad022
  Direction = (0,0,-1)
  Length = 30
  Length2 = 10
  Profile = -> Sketch030
  ReferenceAxis = -> Sketch030 [N_Axis]
  Type = 0
FEATURE [Sketcher::SketchObject] Sketch031
  FullyConstrained = true
  MapMode = 5
  Placement = pos=(0,0,0) rot=(1,0,0;1.5708rad)
  Support = -> [XZ_Plane018]
FEATURE [PartDesign::Body] Body018
  Group = -> [Sketch029,Pad022,Sketch030,Pad023,Sketch031]
  Origin = -> Origin018
  Placement = pos=(49,-16,40) rot=(0,-1,0;1.5708rad)
  Tip = -> Pad023
FEATURE [Part::MultiCommon] Common010
  Shapes = -> [Body018,Pad021]
FEATURE [Sketcher::SketchObject] Sketch032
  FullyConstrained = false
  MapMode = 5
  Placement = pos=(0,0,0) rot=(1,0,0;1.5708rad)
  sketch-geometry (4):
    g0: LineSegment StartX=0.4 StartY=0 StartZ=0 EndX=187.784 EndY=0 EndZ=0
    g1: LineSegment StartX=187.784 StartY=0 StartZ=0 EndX=187.784 EndY=-55.3386 EndZ=0
    g2: LineSegment StartX=187.784 StartY=-55.3386 StartZ=0 EndX=0.4 EndY=-55.3386 EndZ=0
    g3: LineSegment StartX=0.4 StartY=-55.3386 StartZ=0 EndX=0.4 EndY=0 EndZ=0
  constraints (8):
    c: Coincident(g0,g1)
    c: Coincident(g1,g2)
    c: Coincident(g2,g3)
    c: Coincident(g3,g0)
    c: Horizontal(g0)
    c: Horizontal(g2)
    c: Vertical(g1)
    c: Vertical(g3)
FEATURE [Part::Extrusion] Extrude001
  Base = -> Sketch032
  Dir = (0,-1,-2e-16)
  DirMode = 2
  FaceMakerClass = Part::FaceMakerBullseye
  LengthFwd = 43
  LengthRev = 0
  Placement = pos=(49,20,40) rot=(0,-1,0;1.5708rad)
  Solid = true
  Symmetric = false
FEATURE [Sketcher::SketchObject] Sketch033
  FullyConstrained = false
  MapMode = 5
  Support = -> [XY_Plane013]
  sketch-geometry (4):
    g0: LineSegment StartX=-7.74956 StartY=27.0881 StartZ=0 EndX=30.8607 EndY=27.0881 EndZ=0
    g1: LineSegment StartX=30.8607 StartY=27.0881 StartZ=0 EndX=30.8607 EndY=-9.4314 EndZ=0
    g2: LineSegment StartX=30.8607 StartY=-9.4314 StartZ=0 EndX=-7.74956 EndY=-9.4314 EndZ=0
    g3: LineSegment StartX=-7.74956 StartY=-9.4314 StartZ=0 EndX=-7.74956 EndY=27.0881 EndZ=0
  constraints (8):
    c: Coincident(g0,g1)
    c: Coincident(g1,g2)
    c: Coincident(g2,g3)
    c: Coincident(g3,g0)
    c: Horizontal(g0)
    c: Horizontal(g2)
    c: Vertical(g1)
    c: Vertical(g3)
FEATURE [PartDesign::Pad] Pad025
  Direction = (0,0,1)
  Length = 14
  Length2 = 10
  Profile = -> Sketch033
  ReferenceAxis = -> Sketch033 [N_Axis]
  Type = 0
FEATURE [Sketcher::SketchObject] Sketch034
  FullyConstrained = false
  MapMode = 5
  Support = -> [XY_Plane014]
  sketch-geometry (4):
    g0: LineSegment StartX=-7.74956 StartY=27.0881 StartZ=0 EndX=30.8607 EndY=27.0881 EndZ=0
    g1: LineSegment StartX=30.8607 StartY=27.0881 StartZ=0 EndX=30.8607 EndY=-9.4314 EndZ=0
    g2: LineSegment StartX=30.8607 StartY=-9.4314 StartZ=0 EndX=-7.74956 EndY=-9.4314 EndZ=0
    g3: LineSegment StartX=-7.74956 StartY=-9.4314 StartZ=0 EndX=-7.74956 EndY=27.0881 EndZ=0
  constraints (8):
    c: Coincident(g0,g1)
    c: Coincident(g1,g2)
    c: Coincident(g2,g3)
    c: Coincident(g3,g0)
    c: Horizontal(g0)
    c: Horizontal(g2)
    c: Vertical(g1)
    c: Vertical(g3)
FEATURE [PartDesign::Pad] Pad024
  Direction = (0,0,1)
  Length = 14
  Length2 = 10
  Profile = -> Sketch034
  ReferenceAxis = -> Sketch034 [N_Axis]
  Type = 0
FEATURE [PartDesign::Body] Body012
  Group = -> [Sketch034,Pad024]
  Origin = -> Origin012
  Placement = pos=(0,4,110) rot=(0,0.707107,-0.707107;3.14159rad)
  Tip = -> Pad024
FEATURE [Sketcher::SketchObject] Sketch036
  FullyConstrained = false
  MapMode = 5
  Support = -> [XY_Plane021]
  sketch-geometry (30):
    g0: ArcOfCircle CenterX=78.0455 CenterY=-4.69261 CenterZ=0 NormalX=0 NormalY=0 NormalZ=1 AngleXU=0 Radius=0.633228 StartAngle=4.68069 EndAngle=7.80443
    g1-g15: Circle x15 (B-spline internal-alignment scaffolding for g16; pole/knot coordinates omitted)
    g16: BSplineCurve PolesCount=15 KnotsCount=13 Degree=3 IsPeriodic=0
    g17-g29: GeomPoint x13 (B-spline internal-alignment scaffolding for g16; pole/knot coordinates omitted)
  constraints (6):
    c: Weight(g1) = 1
    c: Coincident(g16,g0)
    c: Equal(g1, g2-g15) x14
    c: Coincident(g16,g0)
    c: InternalAlignment(g1-g15 -> g16) x15
    c: InternalAlignment(g17-g29 -> g16) x13
FEATURE [PartDesign::Pad] Pad027
  Direction = (0,0,1)
  Length = 200
  Length2 = 10
  Profile = -> Sketch036
  ReferenceAxis = -> Sketch036 [N_Axis]
  Type = 0
FEATURE [Sketcher::SketchObject] Sketch037
  FullyConstrained = false
  MapMode = 5
  Support = -> [XY_Plane022]
  sketch-geometry (30):
    g0: ArcOfCircle CenterX=78.0455 CenterY=-4.69261 CenterZ=0 NormalX=0 NormalY=0 NormalZ=1 AngleXU=0 Radius=0.633228 StartAngle=4.68069 EndAngle=7.80443
    g1-g15: Circle x15 (B-spline internal-alignment scaffolding for g16; pole/knot coordinates omitted)
    g16: BSplineCurve PolesCount=15 KnotsCount=13 Degree=3 IsPeriodic=0
    g17-g29: GeomPoint x13 (B-spline internal-alignment scaffolding for g16; pole/knot coordinates omitted)
  constraints (6):
    c: Weight(g1) = 1
    c: Coincident(g16,g0)
    c: Equal(g1, g2-g15) x14
    c: Coincident(g16,g0)
    c: InternalAlignment(g1-g15 -> g16) x15
    c: InternalAlignment(g17-g29 -> g16) x13
FEATURE [PartDesign::Pad] Pad028
  Direction = (1,1,1)
  Length = 0.8
  Length2 = 100
  Profile = -> Sketch037
  Type = 0
FEATURE [PartDesign::Body] Body019
  Group = -> [Sketch037,Pad028]
  Origin = -> Origin019
  Placement = pos=(0,0,199.2) rot=(0,0,1;0rad)
  Tip = -> Pad028
FEATURE [Part::Cut] Cut010
  Base = -> Body019
  Tool = -> Box007
FEATURE [PartDesign::Thickness] Thickness003
  Base = -> Pad025 [Face6]
  BaseFeature = -> Pad025
  Intersection = false
  Join = 1
  Mode = 0
  Reversed = true
  SupportTransform = false
  Value = 1.6
FEATURE [Sketcher::SketchObject] Sketch035
  ExternalGeometry = -> [Thickness003]
  FullyConstrained = false
  MapMode = 5
  Placement = pos=(0,0,1.6) rot=(0,0,1;0rad)
  Support = -> [Thickness003]
  sketch-geometry (16):
    g0: LineSegment StartX=-6.14956 StartY=10.9638 StartZ=0 EndX=-0.106128 EndY=10.9638 EndZ=0
    g1: LineSegment StartX=-0.106128 StartY=10.9638 StartZ=0 EndX=-0.106128 EndY=8.15304 EndZ=0
    g2: LineSegment StartX=-0.106128 StartY=8.15304 StartZ=0 EndX=-6.14956 EndY=8.15304 EndZ=0
    g3: LineSegment StartX=-6.14956 StartY=8.15304 StartZ=0 EndX=-6.14956 EndY=10.9638 EndZ=0
    g4: LineSegment StartX=-6.14956 StartY=3.3087 StartZ=0 EndX=0 EndY=3.3087 EndZ=0
    g5: LineSegment StartX=0 StartY=3.3087 StartZ=0 EndX=0 EndY=5.33627 EndZ=0
    g6: LineSegment StartX=0 StartY=5.33627 StartZ=0 EndX=-6.14956 EndY=5.33627 EndZ=0
    g7: LineSegment StartX=-6.14956 StartY=5.33627 StartZ=0 EndX=-6.14956 EndY=3.3087 EndZ=0
    g8: LineSegment StartX=29.2607 StartY=10.6733 StartZ=0 EndX=22.6404 EndY=10.6733 EndZ=0
    g9: LineSegment StartX=22.6404 StartY=10.6733 StartZ=0 EndX=22.6404 EndY=8.47828 EndZ=0
    g10: LineSegment StartX=22.6404 StartY=8.47828 StartZ=0 EndX=29.2607 EndY=8.47828 EndZ=0
    g11: LineSegment StartX=29.2607 StartY=8.47828 StartZ=0 EndX=29.2607 EndY=10.6733 EndZ=0
    g12: LineSegment StartX=29.2607 StartY=5.57967 StartZ=0 EndX=22.6404 EndY=5.57967 EndZ=0
    g13: LineSegment StartX=22.6404 StartY=5.57967 StartZ=0 EndX=22.6404 EndY=3.49718 EndZ=0
    g14: LineSegment StartX=22.6404 StartY=3.49718 StartZ=0 EndX=29.2607 EndY=3.49718 EndZ=0
    g15: LineSegment StartX=29.2607 StartY=3.49718 StartZ=0 EndX=29.2607 EndY=5.57967 EndZ=0
  constraints (37):
    c: Coincident(g0,g1)
    c: Coincident(g1,g2)
    c: Coincident(g2,g3)
    c: Coincident(g3,g0)
    c: Horizontal(g0)
    c: Horizontal(g2)
    c: Vertical(g1)
    c: Vertical(g3)
    c: PointOnObject(g0,g-3)
    c: Coincident(g4,g5)
    c: Coincident(g5,g6)
    c: Coincident(g6,g7)
    c: Coincident(g7,g4)
    c: Horizontal(g4)
    c: Horizontal(g6)
    c: Vertical(g5)
    c: Vertical(g7)
    c: PointOnObject(g4,g-3)
    c: PointOnObject(g5,g-2)
    c: Coincident(g8,g9)
    c: Coincident(g9,g10)
    c: Coincident(g10,g11)
    c: Coincident(g11,g8)
    c: Horizontal(g8)
    c: Horizontal(g10)
    c: Vertical(g9)
    c: Vertical(g11)
    c: PointOnObject(g8,g-4)
    c: Coincident(g12,g13)
    c: Coincident(g13,g14)
    c: Coincident(g14,g15)
    c: Coincident(g15,g12)
    c: Horizontal(g12)
    c: Horizontal(g14)
    c: Vertical(g13)
    c: Vertical(g15)
    c: PointOnObject(g12,g-4)
FEATURE [PartDesign::Pad] Pad026
  BaseFeature = -> Thickness003
  Direction = (0,0,1)
  Length = 12.4
  Length2 = 10
  Profile = -> Sketch035
  ReferenceAxis = -> Sketch035 [N_Axis]
  Type = 0
FEATURE [PartDesign::Body] Body011
  Group = -> [Sketch033,Pad025,Thickness003,Sketch035,Pad026]
  Origin = -> Origin011
  Placement = pos=(0,4,110) rot=(0,-0.707107,0.707107;3.14159rad)
  Tip = -> Pad026
FEATURE [Part::MultiCommon] Common007
  Shapes = -> [Body011,Pad027]
FEATURE [PartDesign::Thickness] Thickness004
  Base = -> BaseFeature001 [Face3,Face2]
  BaseFeature = -> BaseFeature001
  Intersection = false
  Join = 0
  Mode = 1
  SupportTransform = false
  Value = 0.4
FEATURE [PartDesign::Body] Body013
  BaseFeature = -> Cylinder006
  Group = -> [BaseFeature001,Thickness004]
  Origin = -> Origin013
  Placement = pos=(-20,0,0) rot=(0,0,1;0rad)
  Tip = -> Thickness004
FEATURE [PartDesign::Thickness] Thickness005
  Base = -> Pad018 [Face4,Face3]
  BaseFeature = -> Pad018
  Intersection = false
  Join = 0
  Mode = 1
  SupportTransform = false
  Value = 0.4
FEATURE [PartDesign::Body] Body015
  Group = -> [Sketch025,Pad018,Thickness005]
  Origin = -> Origin015
  Tip = -> Thickness005
FEATURE [Part::MultiFuse] Fusion011
  Shapes = -> [Body015,Fusion010]
FEATURE [Part::Cut] Cut006
  Base = -> Fusion011
  Tool = -> Extrude001
FEATURE [Part::MultiFuse] Fusion012
  Shapes = -> [Cut006,Common010]
FEATURE [Part::Cut] Cut007
  Base = -> Fusion012
  Tool = -> Body012
FEATURE [Part::MultiFuse] Fusion009
  Shapes = -> [Common007,Cut007]
FEATURE [Part::Cut] Cut009
  Base = -> Fusion009
  Tool = -> Cylinder007
FEATURE [Part::MultiFuse] Fusion013
  Shapes = -> [Cut010,Cut008,Cut009]
FEATURE [Part::MultiFuse] Fusion014
  Shapes = -> [Body013,Fusion013]
FEATURE [Part::MultiCommon] Common011
  Shapes = -> [Box006,Fusion008]
FEATURE [Part::MultiFuse] Fusion015
  Shapes = -> [Common011,Fusion014]
